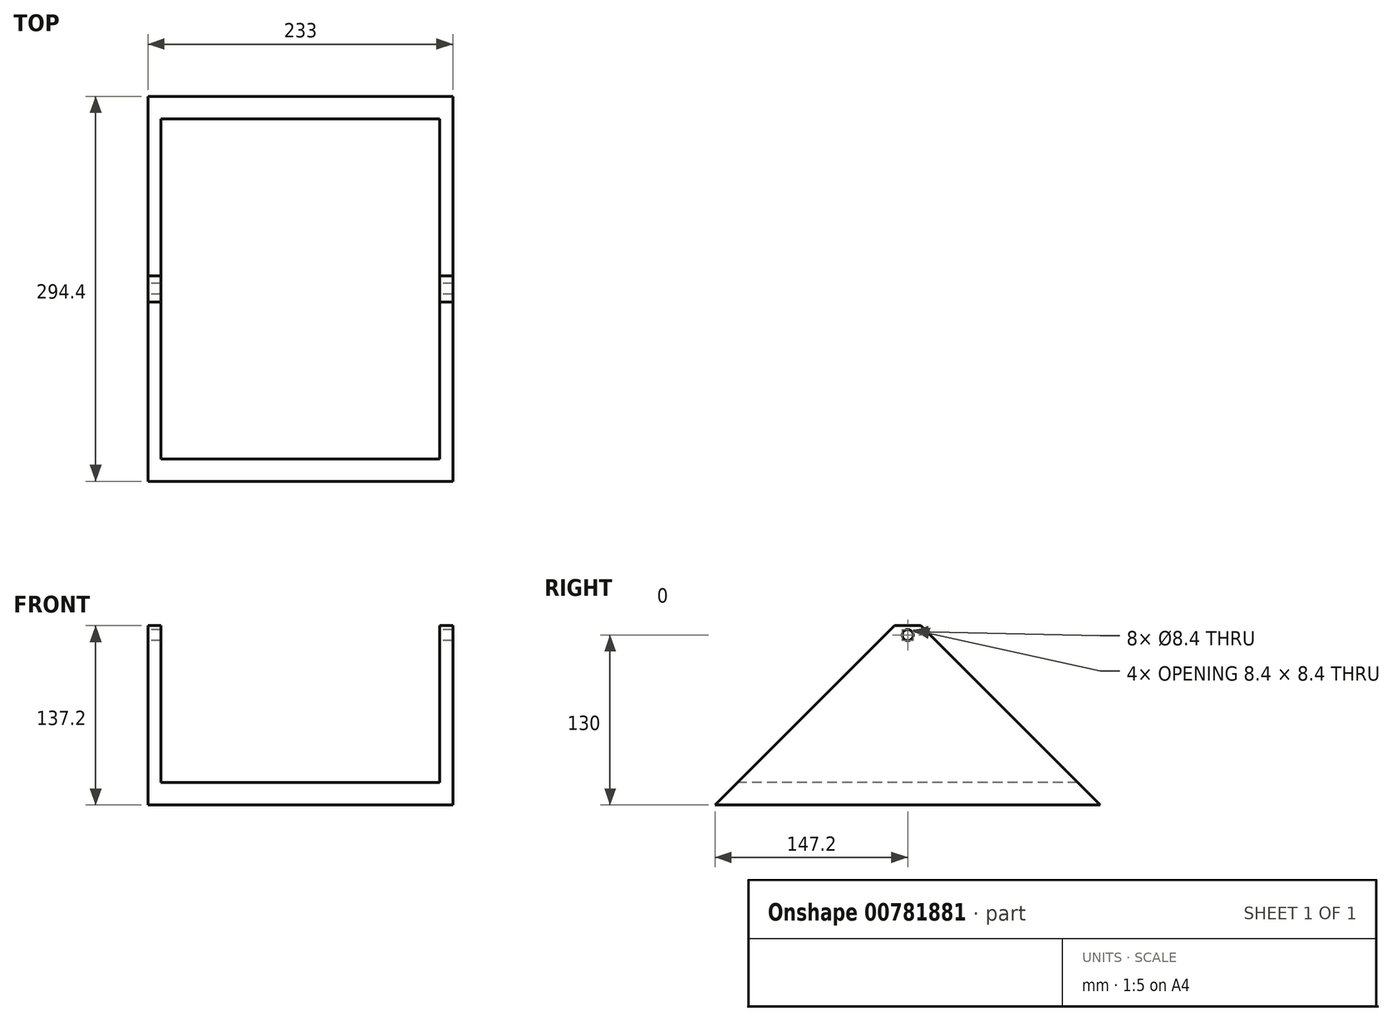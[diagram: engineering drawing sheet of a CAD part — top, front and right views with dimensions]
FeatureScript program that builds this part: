
annotation { "Feature Type Name" : "Feature", "Feature Type Description" : "" }
export const myFeature = defineFeature(function(context is Context, id is Id, definition is map)
    precondition{}
    {
        {
            var Q0;
            Q0=qCreatedBy(makeId("Right.planeOp"),FACE);
            var sketch = newSketch(context, id + "F0", { "sketchPlane" : qUnion([Q0])});
            skLineSegment(sketch, "E0", {"start": v(0, 0) * mm, "end": v(294.4, 0) * mm});
            skLineSegment(sketch, "E1", {"start": v(294.4, 0) * mm, "end": v(157.2, 137.2) * mm});
            skLineSegment(sketch, "E2", {"start": v(157.2, 137.2) * mm, "end": v(137.2, 137.2) * mm});
            skLineSegment(sketch, "E3", {"start": v(137.2, 137.2) * mm, "end": v(0, 0) * mm});
            skLineSegment(sketch, "E4", {"start": v(147.2, 137.2) * mm, "end": v(147.2, 0) * mm, "construction": true});
            skCircle(sketch, "E5", {"center": v(147.2, 130) * mm, "radius": 4.2 * mm});
            skPoint(sketch, "E6", {"position": v(147.2, 134.2) * mm});
            skSolve(sketch);
        }
        {
            var Q0;
            Q0=qSketchRegion(id+"F0",true);
            extrude(context, id + "F1", {"entities" : qUnion([Q0]), "depth" : 233 * mm});
        }
        {
            var Q0;
            Q0=makeQuery(id+"F1.opExtrude","SWEPT_FACE",FACE,{"disambiguationData":[OSD([sQuery(id+"F0.wireOp",EDGE,"E2")])]});
            var sketch = newSketch(context, id + "F2", { "sketchPlane" : qUnion([Q0])});
            skLineSegment(sketch, "E7", {"start": v(116.5, 137.2) * mm, "end": v(116.5, 157.2) * mm, "construction": true});
            skLineSegment(sketch, "E8.rect.bottom", {"start": v(10, 294.4) * mm, "end": v(223, 294.4) * mm});
            skLineSegment(sketch, "E8.rect.top", {"start": v(10, 0) * mm, "end": v(223, 0) * mm});
            skLineSegment(sketch, "E8.rect.left", {"start": v(10, 294.4) * mm, "end": v(10, 0) * mm});
            skLineSegment(sketch, "E8.rect.right", {"start": v(223, 294.4) * mm, "end": v(223, 0) * mm});
            skPoint(sketch, "E8.rect.middle", {"position": v(116.5, 147.2) * mm});
            skSolve(sketch);
        }
        {
            var Q0;
            Q0=qSketchRegion(id+"F2",true);
            extrude(context, id + "F3", {"entities" : qUnion([Q0]), "operationType" : NewBodyOperationType.REMOVE, "oppositeDirection" : true, "depth" : 120 * mm});
        }
    });
